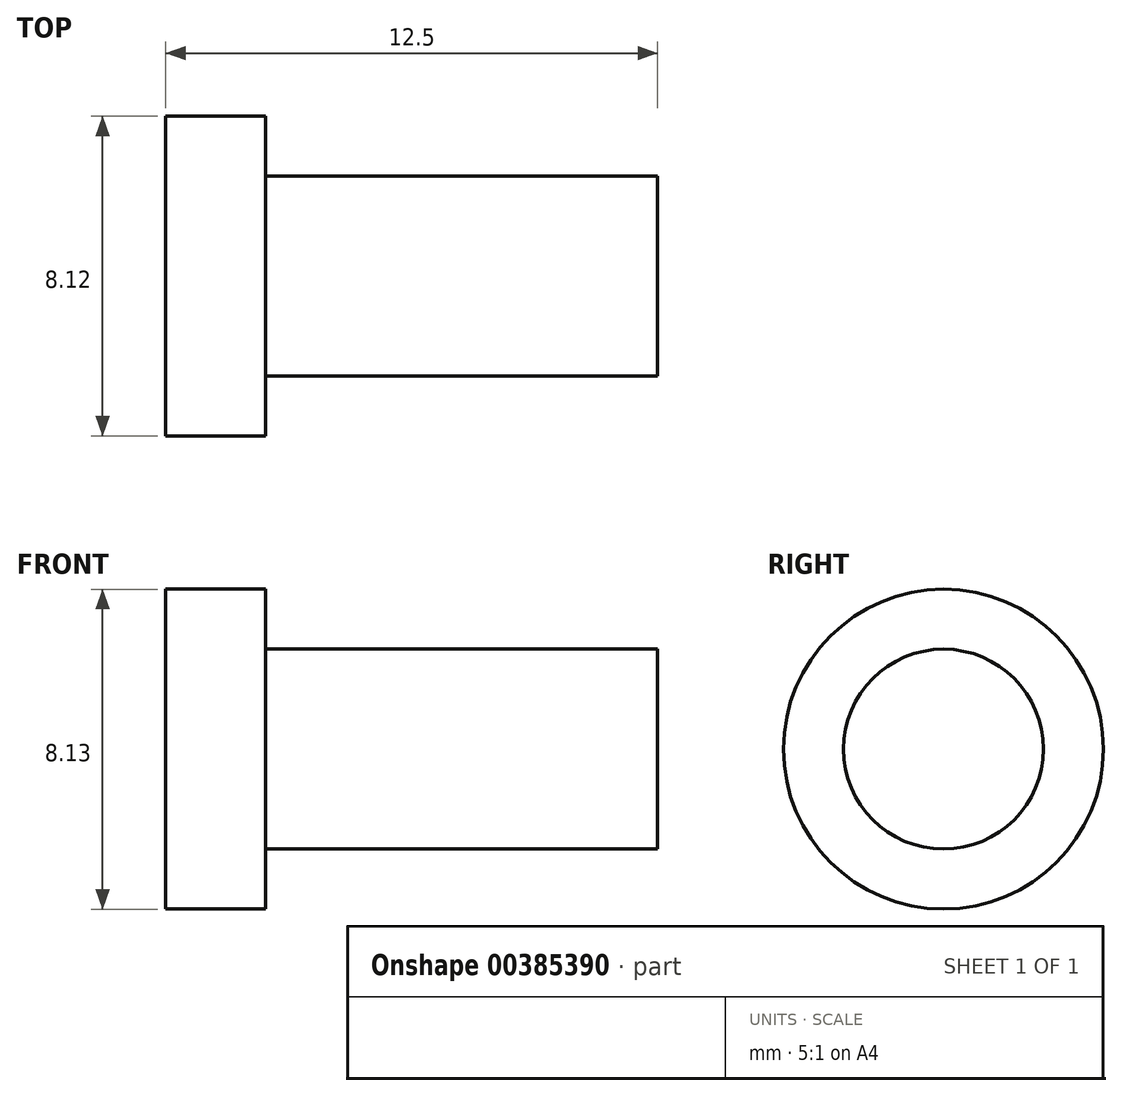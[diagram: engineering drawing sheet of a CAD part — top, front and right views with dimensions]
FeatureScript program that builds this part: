
annotation { "Feature Type Name" : "Feature", "Feature Type Description" : "" }
export const myFeature = defineFeature(function(context is Context, id is Id, definition is map)
    precondition{}
    {
        {
            var Q0;
            Q0=qCreatedBy(makeId("Front.planeOp"),FACE);
            var sketch = newSketch(context, id + "F0", { "sketchPlane" : qUnion([Q0])});
            skLineSegment(sketch, "E0", {"start": v(7.49, 0.34) * mm, "end": v(-2.47, 0.34) * mm});
            skLineSegment(sketch, "E1", {"start": v(-2.47, 0.34) * mm, "end": v(-2.47, 1.86) * mm});
            skLineSegment(sketch, "E2", {"start": v(-2.47, 1.86) * mm, "end": v(-5.01, 1.86) * mm});
            skLineSegment(sketch, "E3", {"start": v(-5.01, 1.86) * mm, "end": v(-5.01, -2.2) * mm});
            skLineSegment(sketch, "E4", {"start": v(-5.01, -2.2) * mm, "end": v(7.49, -2.2) * mm});
            skLineSegment(sketch, "E5", {"start": v(7.49, -2.2) * mm, "end": v(7.49, 0.34) * mm});
            skSolve(sketch);
        }
        {
            var Q0;
            Q0=makeQuery(id+"F0.imprint","IMPRINT",FACE,{"disambiguationData":[TD([[makeQuery(id+"F0.imprint","IMPRINT",EDGE,{"derivedFrom":sQuery(id+"F0.wireOp",EDGE,"E0")}),1.0]])]});
            var Q1;
            Q1=sQuery(id+"F0.wireOp",EDGE,"E4");
            revolve(context, id + "F1", {"entities" : qUnion([Q0]), "axis" : qUnion([Q1]), "revolveType" : RevolveType.FULL});
        }
    });
